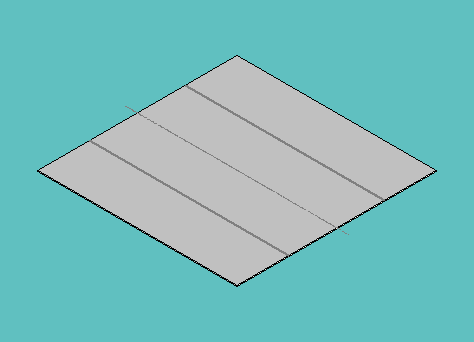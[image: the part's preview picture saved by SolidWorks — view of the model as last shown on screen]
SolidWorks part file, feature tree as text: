
SOLIDWORKS PART (.sldprt)
format: sldprt  version: not decoded by parser v0  size: 267,264 bytes
history: native  units: mm
features: plane x6, sketch x5, extrude x2, material x1 (+11 scaffold rows collapsed)
feature tree (25):
  scaffold x11  (default folders/planes/origin — collapsed)
  material  "Material <not specified>"
  sketch  "Sketch1"  dims[D1=609.6mm D2=609.6mm]
  extrude  "Extrude1"  Depth=3.175mm
  sketch  "straight path"  dims[D1=~479.789027mm D2=~140.399999mm D3=~140.399999mm D4=~69.40042mm D5=~69.40042mm]
  sketch  "strafe path"  dims[c1.D1=~479.789027mm c1.D2=~147.01774mm c1.D3=~147.01774mm c1.D4=~67.74307mm c1.D5=~69.40042mm c2.D1=~67.74307mm]
  sketch  "curved path"  dims[D1=~325.150022mm D2=25.4mm]
  plane  "fwd right"  Offset=140.399999mm
  plane  "fwd left"  Offset=140.399999mm
  plane  "fwd ref plane"  Offset=101.6mm
  plane  "strafe front"
  plane  "strafe back"
  plane  "strafe ref plane"  Offset=101.6mm
  sketch  "sketch3"  dims[D1=~325.150022mm D2=25.4mm]
  extrude  "Extrude2"  Depth=25.4mm
decode coverage: 7 of 7 modeling features carry decoded parameters
note: ~ marks probable driven/reference dimensions
note: suppression state not decoded; provenance and decode notes live in map.json
